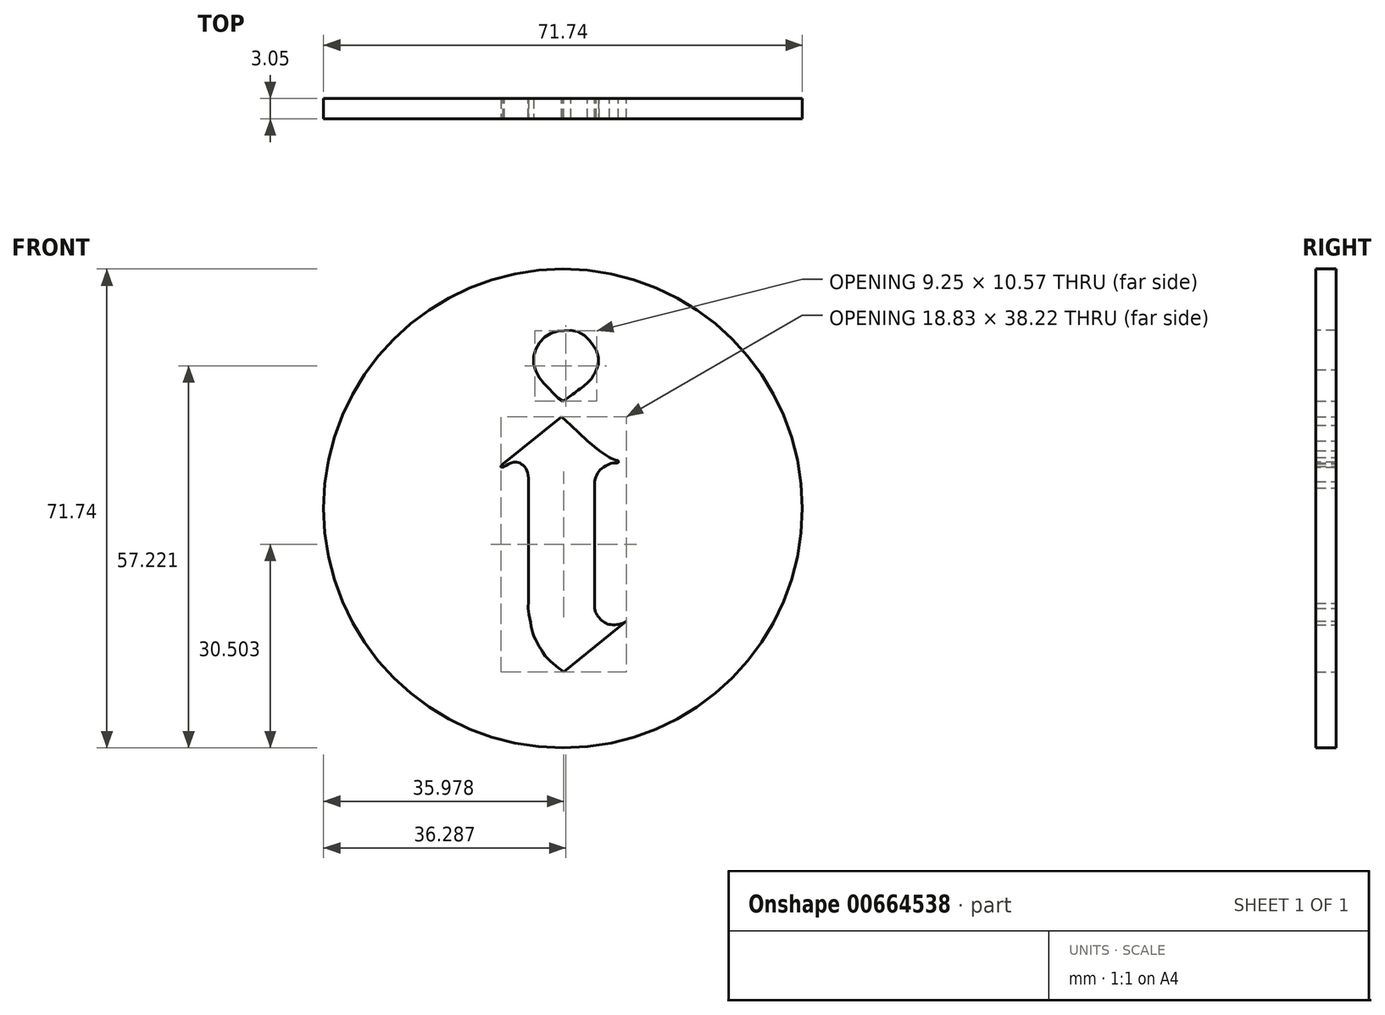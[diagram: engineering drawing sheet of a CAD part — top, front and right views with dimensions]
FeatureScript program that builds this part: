
annotation { "Feature Type Name" : "Feature", "Feature Type Description" : "" }
export const myFeature = defineFeature(function(context is Context, id is Id, definition is map)
    precondition{}
    {
        {
            var Q0;
            Q0=qCreatedBy(makeId("Front.planeOp"),FACE);
            var sketch = newSketch(context, id + "F0", { "sketchPlane" : qUnion([Q0])});
            skCircle(sketch, "E0", {"center": v(-16.54, 0) * mm, "radius": 35.87 * mm});
            skLineSegment(sketch, "E1", {"start": v(-16.45, -24.48) * mm, "end": v(-7.02, -16.88) * mm});
            skLineSegment(sketch, "E2", {"start": v(-7.02, -16.88) * mm, "end": v(-16.45, -24.48) * mm});
            skLineSegment(sketch, "E3", {"start": v(-11.82, 4) * mm, "end": v(-11.82, 0) * mm});
            skLineSegment(sketch, "E4", {"start": v(-11.82, 0) * mm, "end": v(-11.82, -9.13) * mm});
            skLineSegment(sketch, "E5", {"start": v(-11.82, -9.13) * mm, "end": v(-11.82, -14.94) * mm});
            skFitSpline(sketch, "E6", {"points": [v(-11.82, -14.94) * mm, v(-11.57, -15.78) * mm, v(-11.16, -16.33) * mm, v(-10.62, -16.88) * mm, v(-9.98, -17.26) * mm, v(-9.26, -17.4) * mm, v(-8.28, -17.4) * mm, v(-7.83, -17.3) * mm, v(-7.02, -16.88) * mm], "startDerivative": vector(1.4, -6.7) * mm, "endDerivative": vector(6.48, 3.62) * mm});
            skFitSpline(sketch, "E7", {"points": [v(-16.54, 16.06) * mm, v(-15.15, 17.05) * mm, v(-13.45, 18.34) * mm, v(-12.38, 19.33) * mm, v(-11.53, 20.76) * mm], "startDerivative": vector(5.38, 3.74) * mm, "endDerivative": vector(3.24, 6.3) * mm});
            skFitSpline(sketch, "E8", {"points": [v(-11.53, 20.76) * mm, v(-11.22, 21.97) * mm, v(-11.53, 23.66) * mm, v(-12.2, 24.7) * mm, v(-13.1, 25.72) * mm, v(-14.84, 26.62) * mm, v(-16.32, 26.62) * mm, v(-17.7, 26.48) * mm, v(-19.27, 25.68) * mm, v(-20.43, 24.16) * mm, v(-20.97, 22.37) * mm, v(-20.7, 20.76) * mm, v(-19.76, 19.1) * mm, v(-18.5, 17.85) * mm, v(-17.48, 16.73) * mm, v(-16.54, 16.06) * mm], "startDerivative": vector(7.24, 18.92) * mm, "endDerivative": vector(16.87, -10.41) * mm});
            skPoint(sketch, "E9.23.internal.orphan", {"position": v(-16.54, 13.74) * mm});
            skFitSpline(sketch, "E10", {"points": [v(-16.45, -24.48) * mm, v(-17.63, -23.57) * mm, v(-19.06, -22.22) * mm, v(-20.15, -20.6) * mm, v(-20.98, -18.87) * mm, v(-21.43, -16.96) * mm, v(-21.73, -15.11) * mm, v(-21.73, -14.21) * mm], "startDerivative": vector(-8.58, 6.35) * mm, "endDerivative": vector(0.43, 7.88) * mm});
            skLineSegment(sketch, "E11", {"start": v(-21.73, -14.21) * mm, "end": v(-21.73, 3.08) * mm});
            skPoint(sketch, "E12.1.internal.orphan", {"position": v(-21.73, 4.7) * mm});
            skLineSegment(sketch, "E13", {"start": v(-16.78, 13.74) * mm, "end": v(-25.5, 6.66) * mm});
            skFitSpline(sketch, "E14", {"points": [v(-25.5, 6.66) * mm, v(-25.83, 6.37) * mm, v(-25.83, 6.2) * mm, v(-25.72, 6.14) * mm, v(-25.5, 6.2) * mm, v(-25.35, 6.3) * mm], "startDerivative": vector(-1.47, -1) * mm, "endDerivative": vector(0.74, 0.52) * mm});
            skFitSpline(sketch, "E15", {"points": [v(-25.35, 6.3) * mm, v(-24.4, 6.78) * mm, v(-23.95, 6.93) * mm, v(-23.3, 6.9) * mm, v(-22.6, 6.55) * mm, v(-22.2, 6.14) * mm, v(-21.73, 4.7) * mm, v(-21.73, 3.08) * mm], "startDerivative": vector(6.78, 3.5) * mm, "endDerivative": vector(-0.64, -8.3) * mm});
            skLineSegment(sketch, "E16", {"start": v(-16.78, 13.74) * mm, "end": v(-15.35, 12.49) * mm});
            skLineSegment(sketch, "E17", {"start": v(-15.35, 12.49) * mm, "end": v(-12.91, 10.09) * mm});
            skLineSegment(sketch, "E18", {"start": v(-12.91, 10.09) * mm, "end": v(-11.1, 8.66) * mm});
            skLineSegment(sketch, "E19", {"start": v(-11.1, 8.66) * mm, "end": v(-9.6, 7.65) * mm});
            skFitSpline(sketch, "E20", {"points": [v(-9.6, 7.65) * mm, v(-8.84, 7.33) * mm, v(-8.27, 7.15) * mm, v(-8.24, 6.93) * mm, v(-8.37, 6.82) * mm, v(-8.73, 6.83) * mm, v(-9.38, 6.73) * mm, v(-9.96, 6.48) * mm, v(-10.56, 6.1) * mm, v(-11.17, 5.54) * mm, v(-11.52, 4.91) * mm, v(-11.82, 4) * mm], "startDerivative": vector(6.7, -3.54) * mm, "endDerivative": vector(-2.34, -8.18) * mm});
            skSolve(sketch);
        }
        {
            var Q0;
            Q0 = qSketchRegion(id + "F0", true);
            extrude(context, id + "F1", {"entities" : qUnion([Q0]), "depth" : 3.05 * mm, "offsetDistance" : 25.4 * mm});
        }
    });
